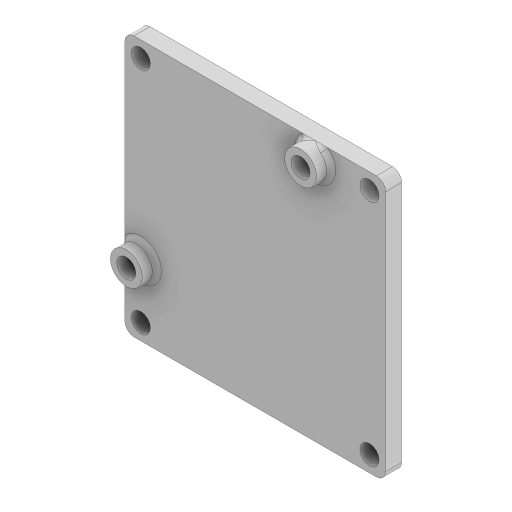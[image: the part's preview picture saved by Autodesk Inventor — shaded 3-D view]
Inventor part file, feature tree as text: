
AUTODESK INVENTOR PART (.ipt)
format: ipt  version: 2023 (Build 270158000, 158)  size: 175,616 bytes
history: native  units: mm
features: sketch x2, extrude x2, fillet x2
ambient origin geometry x8: Origin, YZ Plane, XZ Plane, XY Plane, X Axis, Y Axis, Z Axis, Center Point
bodies: Solid1 (feature_tree)
feature tree (6):
  sketch  "Sketch1"  dims[d0=57.0mm d1=57.0mm]
  extrude  "Extrusion1"  Depth=57.0mm
  extrude  "Extrusion2"  Depth=2.0mm
  sketch  "Sketch Driven Pattern1"  dims[d2=50.0mm d3=50.0mm d4=4.15mm d5=4.15mm d6=4.15mm d7=4.15mm d8=38.1mm d9=38.1mm d10=4.15mm d12=4.15mm d13=7.0mm d14=3.5mm d15=0.0mm d16=3.175mm d17=0.0mm d19=1.0mm d20=2.0mm]
  fillet  "Fillet2"  Radius=4.15mm
  fillet  "Fillet3"  Radius=4.15mm
